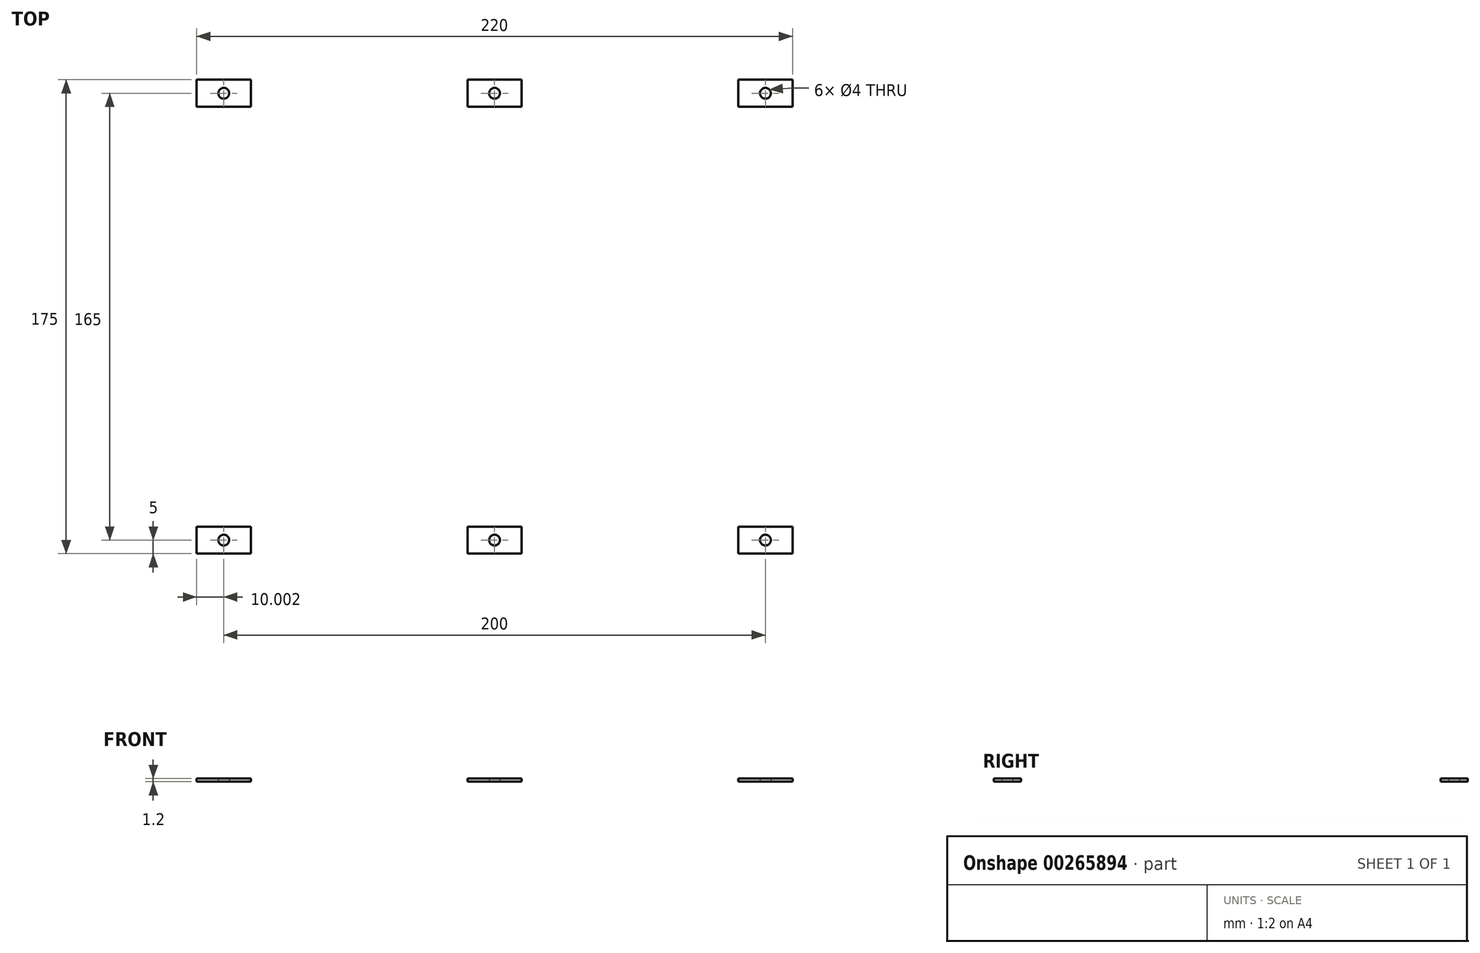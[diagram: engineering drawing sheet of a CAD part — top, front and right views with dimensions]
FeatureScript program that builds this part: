
annotation { "Feature Type Name" : "Feature", "Feature Type Description" : "" }
export const myFeature = defineFeature(function(context is Context, id is Id, definition is map)
    precondition{}
    {
        {
            var Q0;
            Q0=qCreatedBy(makeId("Top.planeOp"),FACE);
            var sketch = newSketch(context, id + "F0", { "sketchPlane" : qUnion([Q0])});
            skLineSegment(sketch, "E0.bottom", {"start": v(-119.07, 87.5) * mm, "end": v(-99.07, 87.5) * mm});
            skLineSegment(sketch, "E0.top", {"start": v(-119.07, 77.5) * mm, "end": v(-99.07, 77.5) * mm});
            skLineSegment(sketch, "E0.left", {"start": v(-119.07, 87.5) * mm, "end": v(-119.07, 77.5) * mm});
            skLineSegment(sketch, "E0.right", {"start": v(-99.07, 87.5) * mm, "end": v(-99.07, 77.5) * mm});
            skLineSegment(sketch, "E1.bottom", {"start": v(80.93, 87.5) * mm, "end": v(100.93, 87.5) * mm});
            skLineSegment(sketch, "E1.top", {"start": v(80.93, 77.5) * mm, "end": v(100.93, 77.5) * mm});
            skLineSegment(sketch, "E1.left", {"start": v(80.93, 87.5) * mm, "end": v(80.93, 77.5) * mm});
            skLineSegment(sketch, "E1.right", {"start": v(100.93, 87.5) * mm, "end": v(100.93, 77.5) * mm});
            skLineSegment(sketch, "E2.bottom", {"start": v(-19.07, 87.5) * mm, "end": v(0.93, 87.5) * mm});
            skLineSegment(sketch, "E2.top", {"start": v(-19.07, 77.5) * mm, "end": v(0.93, 77.5) * mm});
            skLineSegment(sketch, "E2.left", {"start": v(-19.07, 87.5) * mm, "end": v(-19.07, 77.5) * mm});
            skLineSegment(sketch, "E2.right", {"start": v(0.93, 87.5) * mm, "end": v(0.93, 77.5) * mm});
            skLineSegment(sketch, "E3.bottom", {"start": v(-119.07, -77.5) * mm, "end": v(-99.07, -77.5) * mm});
            skLineSegment(sketch, "E3.top", {"start": v(-119.07, -87.5) * mm, "end": v(-99.07, -87.5) * mm});
            skLineSegment(sketch, "E3.left", {"start": v(-119.07, -77.5) * mm, "end": v(-119.07, -87.5) * mm});
            skLineSegment(sketch, "E3.right", {"start": v(-99.07, -77.5) * mm, "end": v(-99.07, -87.5) * mm});
            skLineSegment(sketch, "E4.bottom", {"start": v(-19.07, -77.5) * mm, "end": v(0.93, -77.5) * mm});
            skLineSegment(sketch, "E4.top", {"start": v(-19.07, -87.5) * mm, "end": v(0.93, -87.5) * mm});
            skLineSegment(sketch, "E4.left", {"start": v(-19.07, -77.5) * mm, "end": v(-19.07, -87.5) * mm});
            skLineSegment(sketch, "E4.right", {"start": v(0.93, -77.5) * mm, "end": v(0.93, -87.5) * mm});
            skLineSegment(sketch, "E5.bottom", {"start": v(80.93, -77.5) * mm, "end": v(100.93, -77.5) * mm});
            skLineSegment(sketch, "E5.top", {"start": v(80.93, -87.5) * mm, "end": v(100.93, -87.5) * mm});
            skLineSegment(sketch, "E5.left", {"start": v(80.93, -77.5) * mm, "end": v(80.93, -87.5) * mm});
            skLineSegment(sketch, "E5.right", {"start": v(100.93, -77.5) * mm, "end": v(100.93, -87.5) * mm});
            skCircle(sketch, "E6", {"center": v(-109.07, 82.5) * mm, "radius": 2 * mm});
            skPoint(sketch, "E6.centerSnap0", {"position": v(-109.07, 77.5) * mm});
            skLineSegment(sketch, "E7", {"start": v(-109.07, 82.5) * mm, "end": v(104.92, 82.5) * mm, "construction": true});
            skPoint(sketch, "E7.endSnap0", {"position": v(100.93, 82.5) * mm});
            skLineSegment(sketch, "E8", {"start": v(-119.07, -82.5) * mm, "end": v(103.48, -82.5) * mm, "construction": true});
            skPoint(sketch, "E8.endSnap0", {"position": v(100.93, -82.5) * mm});
            skCircle(sketch, "E9", {"center": v(-9.07, 82.5) * mm, "radius": 2 * mm});
            skCircle(sketch, "E10", {"center": v(90.93, 82.5) * mm, "radius": 2 * mm});
            skCircle(sketch, "E11", {"center": v(90.93, -82.5) * mm, "radius": 2 * mm});
            skCircle(sketch, "E12", {"center": v(-9.07, -82.5) * mm, "radius": 2 * mm});
            skPoint(sketch, "E12.centerSnap0", {"position": v(-9.07, -77.5) * mm});
            skCircle(sketch, "E13", {"center": v(-109.07, -82.5) * mm, "radius": 2 * mm});
            skSolve(sketch);
        }
        {
            var Q0;
            Q0 = qSketchRegion(id + "F0", true);
            extrude(context, id + "F1", {"entities" : qUnion([Q0]), "depth" : 1.2 * mm});
        }
    });
